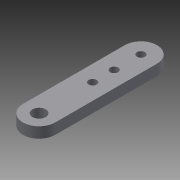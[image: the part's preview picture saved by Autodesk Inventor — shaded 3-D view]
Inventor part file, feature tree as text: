
AUTODESK INVENTOR PART (.ipt)
format: ipt  version: 2013 (Build 170138000, 138)  size: 88,576 bytes
history: native  units: mm
features: extrude x1, sketch x1
ambient origin geometry x8: Origin, YZ Plane, XZ Plane, XY Plane, X Axis, Y Axis, Z Axis, Center Point
bodies: Solid1 (feature_tree)
feature tree (2):
  extrude  "Extrusion1"  Depth=38.0mm
  sketch  "Sketch1"  dims[d0=12.0mm d1=38.0mm d2=3.0mm d3=5.0mm d4=4.0mm d5=0.0mm d6=3.0mm d7=20.0mm d8=3.0mm d9=10.0mm]
